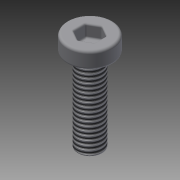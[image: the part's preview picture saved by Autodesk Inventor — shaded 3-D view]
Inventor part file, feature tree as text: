
AUTODESK INVENTOR PART (.ipt)
format: ipt  version: 2013 (Build 170138000, 138)  size: 158,208 bytes
history: native  units: mm
features: extrude x3, sketch x3, fillet x2, other x1, thread x1
ambient origin geometry x1: Origin
feature tree (10):
  other  "ソリッド1"
  extrude  "押し出し1"  Depth=5.5mm
  extrude  "押し出し2"  Depth=2.0mm TaperAngle=0.0deg
  extrude  "押し出し3"  Depth=3.0mm
  fillet  "フィレット1"  Radius=10.0mm
  fillet  "フィレット2"  Radius=1.25mm
  thread  "ねじ2"
  sketch  "スケッチ1"
  sketch  "スケッチ2"
  sketch  "スケッチ3"
